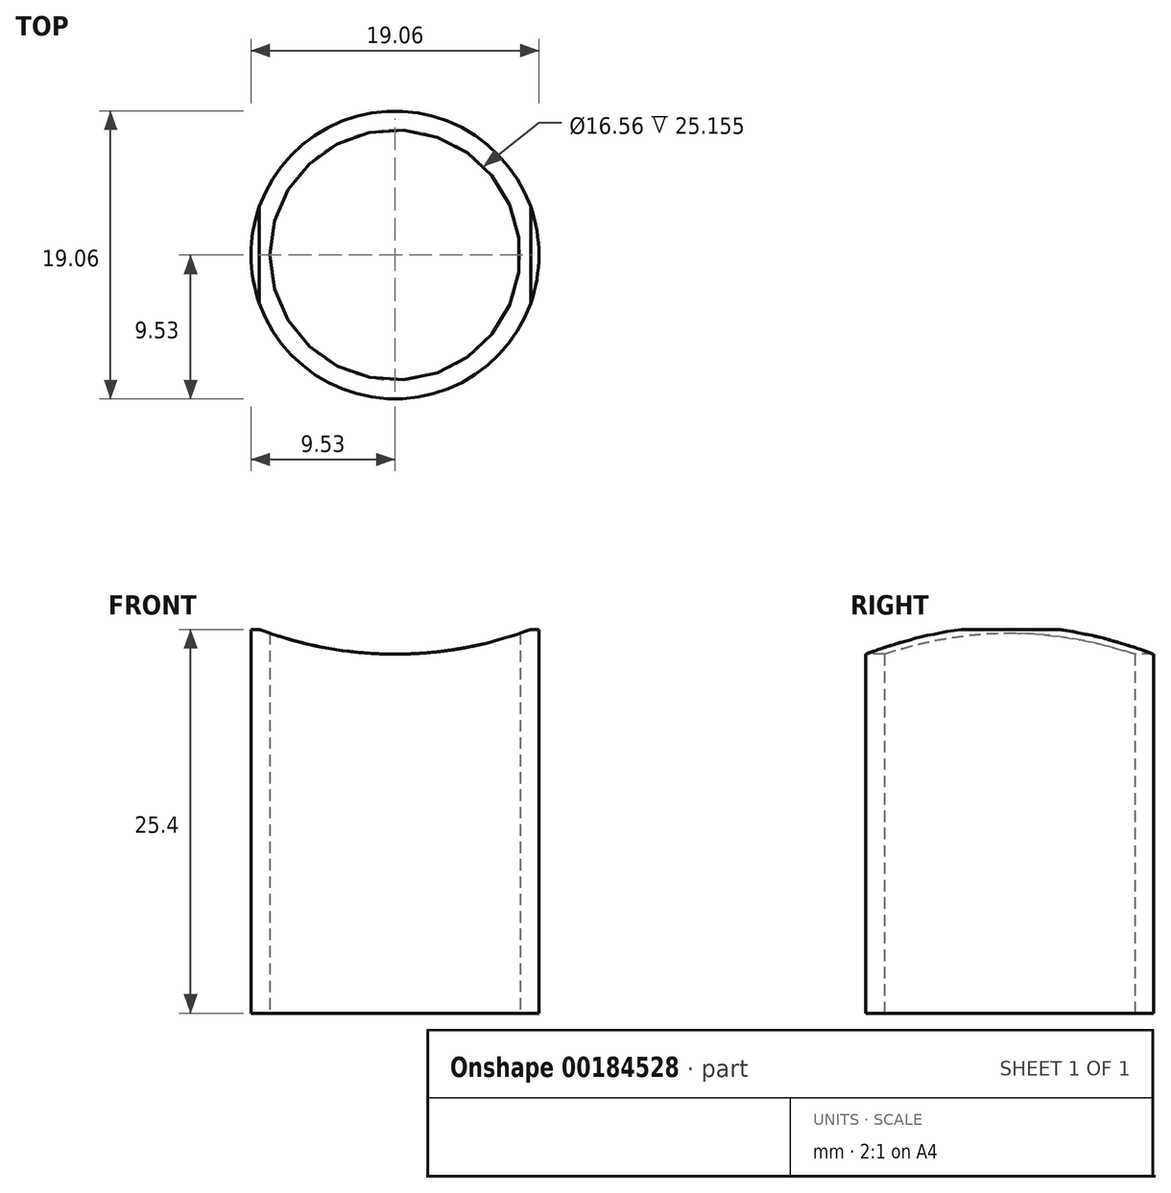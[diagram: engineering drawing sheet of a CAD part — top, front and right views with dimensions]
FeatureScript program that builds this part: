
annotation { "Feature Type Name" : "Feature", "Feature Type Description" : "" }
export const myFeature = defineFeature(function(context is Context, id is Id, definition is map)
    precondition{}
    {
        {
            var Q0;
            Q0=qCreatedBy(makeId("Top.planeOp"),FACE);
            var sketch = newSketch(context, id + "F0", { "sketchPlane" : qUnion([Q0])});
            skCircle(sketch, "E0", {"center": v(0, 0) * mm, "radius": 9.53 * mm});
            skCircle(sketch, "E1.0", {"center": v(0, 0) * mm, "radius": 8.28 * mm});
            skSolve(sketch);
        }
        {
            var Q0;
            Q0 = qSketchRegion(id + "F0", true);
            extrude(context, id + "F1", {"entities" : qUnion([Q0]), "endBound" : BoundingType.SYMMETRIC, "depth" : 25.4 * mm});
        }
        {
            var Q0;
            Q0=qCreatedBy(makeId("Front.planeOp"),FACE);
            var sketch = newSketch(context, id + "F2", { "sketchPlane" : qUnion([Q0])});
            skLineSegment(sketch, "E2", {"start": v(-38.15, 36.46) * mm, "end": v(38.15, 36.46) * mm});
            skCircle(sketch, "E3", {"center": v(0, 36.46) * mm, "radius": 25.4 * mm});
            skSolve(sketch);
        }
        {
            var Q0;
            {var subQ0=sQuery(id+"F2.wireOp",EDGE,"E3");var subQ1=sQuery(id+"F2.wireOp",EDGE,"E2");var subQ2=makeQuery(id+"F2.imprint","INTERSECT",VERTEX,{"disambiguationData":[OD(0.0)],"derivedFrom":[subQ1,subQ0]});Q0=makeQuery(id+"F2.imprint","IMPRINT",FACE,{"disambiguationData":[TD([[makeQuery(id+"F2.imprint","IMPRINT",EDGE,{"disambiguationData":[TD([[subQ2,-1.0]])],"derivedFrom":subQ1}),-1.0]])]});}
            extrude(context, id + "F3", {"entities" : qUnion([Q0]), "operationType" : NewBodyOperationType.REMOVE, "endBound" : BoundingType.SYMMETRIC, "oppositeDirection" : true, "depth" : 25.4 * mm});
        }
    });
